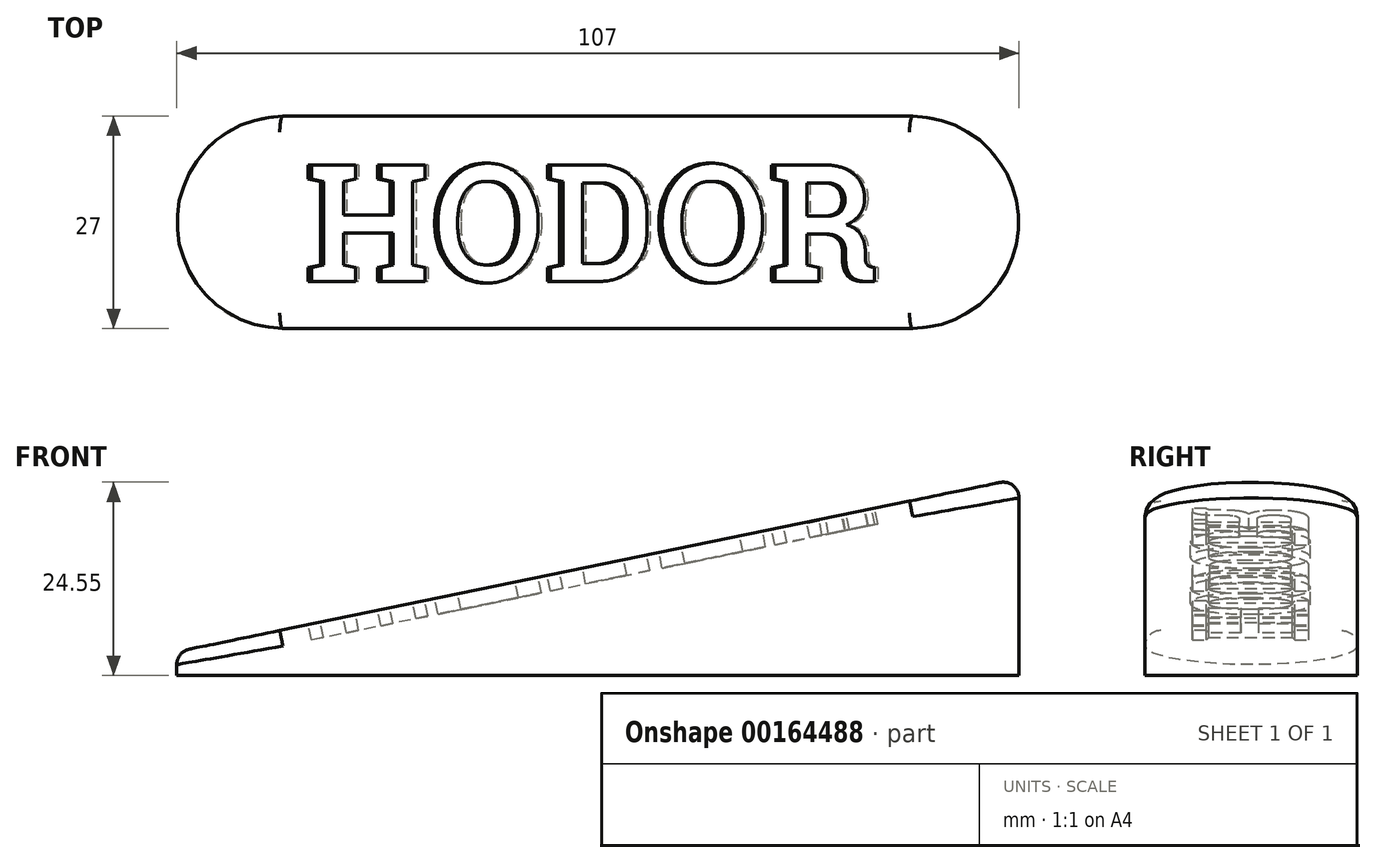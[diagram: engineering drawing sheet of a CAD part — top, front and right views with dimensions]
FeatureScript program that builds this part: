
annotation { "Feature Type Name" : "Feature", "Feature Type Description" : "" }
export const myFeature = defineFeature(function(context is Context, id is Id, definition is map)
    precondition{}
    {
        {
            var Q0;
            Q0=qCreatedBy(makeId("Top.planeOp"),FACE);
            var sketch = newSketch(context, id + "F0", { "sketchPlane" : qUnion([Q0])});
            skLineSegment(sketch, "E0", {"start": v(-40, 0) * mm, "end": v(40, 0) * mm});
            skArc(sketch, "E1.0.startCap", {"start": v(-40, -13.5) * mm, "mid": v(-53.5, 0) * mm, "end": v(-40, 13.5) * mm});
            skArc(sketch, "E1.0.endCap", {"start": v(40, 13.5) * mm, "mid": v(53.5, 0) * mm, "end": v(40, -13.5) * mm});
            skLineSegment(sketch, "E1.0.left", {"start": v(-40, 13.5) * mm, "end": v(40, 13.5) * mm});
            skLineSegment(sketch, "E1.0.right", {"start": v(-40, -13.5) * mm, "end": v(40, -13.5) * mm});
            skSolve(sketch);
        }
        {
            var Q0;
            Q0 = qSketchRegion(id + "F0", true);
            extrude(context, id + "F1", {"entities" : qUnion([Q0]), "depth" : 25 * mm});
        }
        {
            var Q0;
            Q0=qCreatedBy(makeId("Front.planeOp"),FACE);
            var sketch = newSketch(context, id + "F2", { "sketchPlane" : qUnion([Q0])});
            skLineSegment(sketch, "E2", {"start": v(-53.5, 3) * mm, "end": v(53.5, 25) * mm});
            skLineSegment(sketch, "E3", {"start": v(53.5, 25) * mm, "end": v(-53.5, 25) * mm});
            skLineSegment(sketch, "E4", {"start": v(-53.5, 25) * mm, "end": v(-53.5, 3) * mm});
            skSolve(sketch);
        }
        {
            var Q0;
            Q0 = qSketchRegion(id + "F2", true);
            extrude(context, id + "F3", {"entities" : qUnion([Q0]), "operationType" : NewBodyOperationType.REMOVE, "oppositeDirection" : true, "depth" : 25 * mm, "hasSecondDirection" : true, "secondDirectionOppositeDirection" : false, "secondDirectionDepth" : 25 * mm});
        }
        {
            var Q0;
            Q0=makeQuery(id+"F3.boolean.opBoolean","COPY",FACE,{"derivedFrom":makeQuery(id+"F3.opExtrude","SWEPT_FACE",FACE,{"disambiguationData":[OSD([sQuery(id+"F2.wireOp",EDGE,"E2")])]})});
            fillet(context, id + "F4", {"entities" : qUnion([Q0]), "radius" : 2 * mm, "tangentPropagation" : true, "allowEdgeOverflow" : false});
        }
        {
            var Q0;
            Q0=makeQuery(id+"F3.boolean.opBoolean","COPY",FACE,{"derivedFrom":makeQuery(id+"F3.opExtrude","SWEPT_FACE",FACE,{"disambiguationData":[OSD([sQuery(id+"F2.wireOp",EDGE,"E2")])]})});
            var sketch = newSketch(context, id + "F5", { "sketchPlane" : qUnion([Q0])});
            skText(sketch, "E5", { "text": "HODOR", "fontName": "RobotoSlab-Bold.ttf"});
            const initialGuessF5  = {"E5": [-0.0353, -0.0075, 1, 0, 0.015]};
            skSetInitialGuess(sketch, initialGuessF5);
            skSolve(sketch);
        }
        {
            var Q0;
            Q0 = qSketchRegion(id + "F5", true);
            extrude(context, id + "F6", {"entities" : qUnion([Q0]), "operationType" : NewBodyOperationType.REMOVE, "oppositeDirection" : true, "depth" : 2 * mm});
        }
    });
